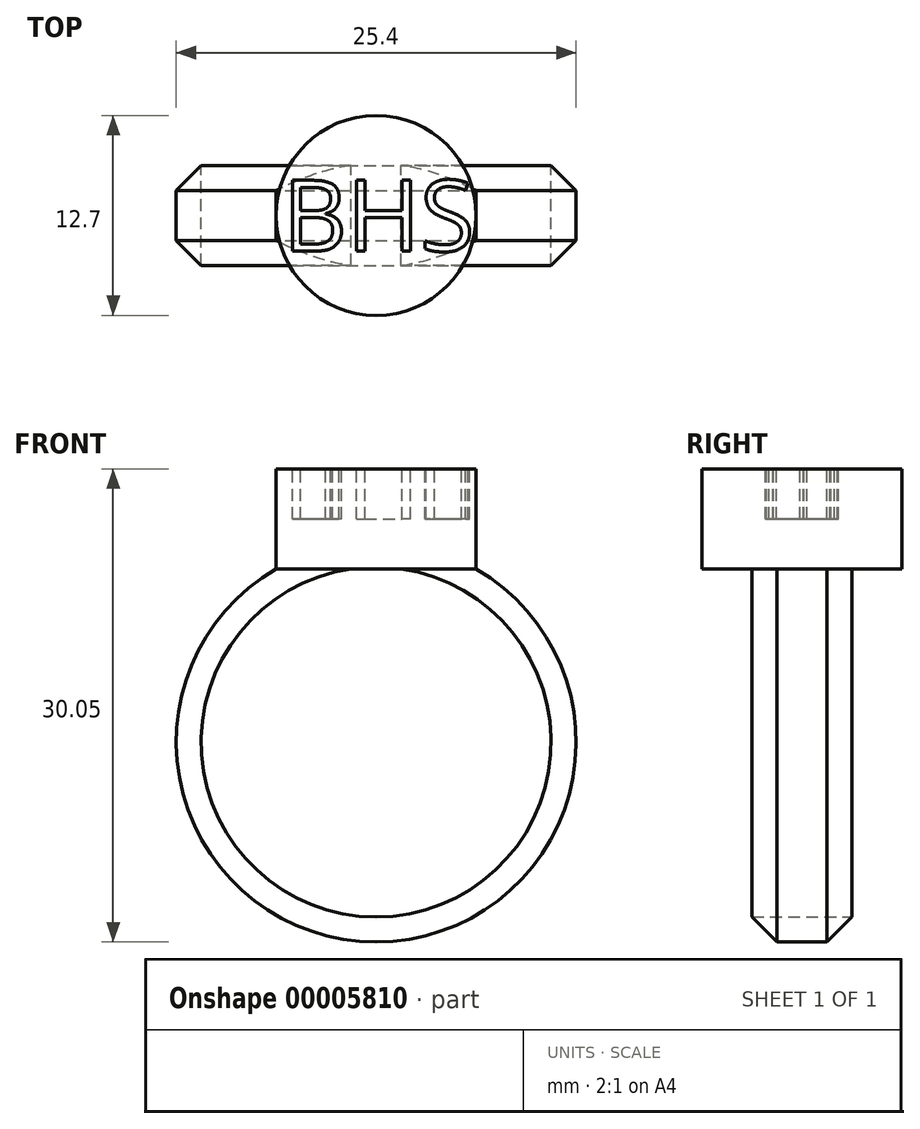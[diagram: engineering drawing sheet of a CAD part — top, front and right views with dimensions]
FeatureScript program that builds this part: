
annotation { "Feature Type Name" : "Feature", "Feature Type Description" : "" }
export const myFeature = defineFeature(function(context is Context, id is Id, definition is map)
    precondition{}
    {
        {
            var Q0;
            Q0=qCreatedBy(makeId("Top.planeOp"),FACE);
            var sketch = newSketch(context, id + "F0", { "sketchPlane" : qUnion([Q0])});
            skCircle(sketch, "E0", {"center": v(0, 0) * mm, "radius": 6.35 * mm});
            skSolve(sketch);
        }
        {
            var Q0;
            Q0=qCreatedBy(makeId("Top.planeOp"),FACE);
            var sketch = newSketch(context, id + "F5", { "sketchPlane" : qUnion([Q0])});
            skText(sketch, "E1", { "text": "BHS", "fontName": "OpenSans-Regular.ttf"});
            const initialGuessFC6Tdjml7Fn8M5UdF_0  = {"E1": [-0.00593, -0.00226, 1, 0, 0.00453]};
            skSetInitialGuess(sketch, initialGuessFC6Tdjml7Fn8M5UdF_0);
            skSolve(sketch);
        }
        {
            var Q0;
            Q0=makeQuery(id+"F0.imprint","IMPRINT",FACE,{"disambiguationData":[TD([[makeQuery(id+"F0.imprint","IMPRINT",EDGE,{"derivedFrom":sQuery(id+"F0.wireOp",EDGE,"E0")}),1.0]])]});
            extrude(context, id + "F1", {"entities" : qUnion([Q0]), "oppositeDirection" : true, "depth" : 6.35 * mm});
        }
        {
            var Q0;
            Q0 = qSketchRegion(id + "F5", true);
            extrude(context, id + "F2", {"entities" : qUnion([Q0]), "operationType" : NewBodyOperationType.REMOVE, "oppositeDirection" : true, "depth" : 3.17 * mm});
        }
        {
            var Q0;
            Q0=qCreatedBy(makeId("Front.planeOp"),FACE);
            var sketch = newSketch(context, id + "F3", { "sketchPlane" : qUnion([Q0])});
            skCircle(sketch, "E2", {"center": v(0, -17.35) * mm, "radius": 12.7 * mm});
            skLineSegment(sketch, "E3.0.0", {"start": v(6.35, -6.35) * mm, "end": v(-6.35, -6.35) * mm});
            skCircle(sketch, "E4", {"center": v(0, -17.35) * mm, "radius": 11.11 * mm});
            skSolve(sketch);
        }
        {
            var Q0;
            {var subQ1=sQuery(id+"F3.wireOp",EDGE,"E3.0.0");var subQ4=sQuery(id+"F3.wireOp",EDGE,"E2");var subQ6=makeQuery(id+"F3.imprint","INTERSECT",VERTEX,{"disambiguationData":[OD(0.0)],"derivedFrom":[subQ4,subQ1]});Q0=makeQuery(id+"F3.imprint","IMPRINT",FACE,{"disambiguationData":[TD([[makeQuery(id+"F3.imprint","IMPRINT",EDGE,{"disambiguationData":[TD([[subQ6,1.0]])],"derivedFrom":subQ4}),1.0]])]});}
            extrude(context, id + "F4", {"entities" : qUnion([Q0]), "operationType" : NewBodyOperationType.ADD, "endBound" : BoundingType.SYMMETRIC, "depth" : 6.35 * mm});
        }
        {
            var Q0;
            Q0=makeQuery(id+"F4.opExtrude","CAP_EDGE",EDGE,{"disambiguationData":[OSD([sQuery(id+"F3.wireOp",EDGE,"E2")])],"isStart":false});
            var Q1;
            Q1=makeQuery(id+"F4.opExtrude","CAP_EDGE",EDGE,{"disambiguationData":[OSD([sQuery(id+"F3.wireOp",EDGE,"E2")])],"isStart":true});
            chamfer(context, id + "F6", {"entities" : qUnion([Q0, Q1]), "width" : 1.59 * mm, "tangentPropagation" : true});
        }
    });
